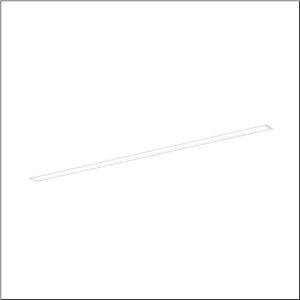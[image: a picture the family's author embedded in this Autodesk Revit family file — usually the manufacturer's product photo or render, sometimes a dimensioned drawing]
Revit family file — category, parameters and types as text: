
# Revit family: silica_21_51mx13tbt5w
name_source: partatom
category: Lighting Fixtures
units: mm (PartAtom-declared; Revit-internal decimal feet)

## family parameters
Cut with Voids When Loaded = No
Host = Face
Light Source = No
Part Type = Normal
Room Calculation Point = No
Round Connector Dimension = Use Diameter
Shared = No

## types (1)
- --- (1 x LED, 4030 lm, 40.5 W, 6500K)
    Apparent Load = 41 VA
    CIE Flux Codes = 78 96 99 100 100
    Color Rendering = 80
    Color Temperature = 6500K
    Default Elevation = 1800 mm
    Description = Silica 21, office luminaire, primary optical cover: prismatic diffuser, of PMMA, CAT 2 (L<= 3000cd/m²), light emission: direct distribution, primary light characteristic: symmetric, installation type: recessed, LED, rated luminous flux: 4.030lm, luminous efficacy: 95lm/W, light colour: 8tw, colour temperature: 2700..6500K, control gear: DALI DT8, with terminal, 3+2-pole, max. 2.5mm², mains connection: 220..240V, AC, 50/60Hz, rated input power: 42.6W, luminaire housing, of aluminium, traffic white (RAL 9016), length: 1.528mm, width: 79mm, height: 53mm, protection rating (complete): IP20, insulation class (complete): insulation class I (protective earthing), certification: CE, ENEC, VDE, permissible operating ambient temperature: 0..+35°C, standard: EN 50419, packaging unit: 1 piece
    Height = 0 mm  [stored 0 ft]
    Lamp = 1 x LED
    Lamp Light Flux = 4030 lm
    Lamp Power = 40.5 W
    Lamp count = 1
    Length = 1527 mm
    Luminous efficacy = 100 lm/W
    Manufacturer = Siteco
    ModVariant = No
    Model = 51MX13TBT5W
    Mounting Place = Ceiling
    Mounting Type = Recessed
    Number of Poles = 1
    OnlyDefault = Yes
    Power Factor = 1
    Product Name = Silica 21
    Product group = office luminaire | ceiling recessed
    ProductGroupID = 400
    Protection Class = Protection class I
    Protection Degree = IP 20
    RLX_Detail_Level = 1
    RLX_Emergency_Light_Flux = 0 lm
    RLX_Emergency_Type = 0
    RLX_Emergency_Type_DB = No
    RlxData = <blob elided: 10977 chars, md5=a58d0484>
    Socket = socket
    Standby Power = 0 W
    System Light Flux = 4030 lm
    System Power = 41 W
    Type Comments = individual setting
    Type Image = l_1251692.jpg
    URL = http://relux.com
    VarID = @adj_140899
    Voltage = 0 V
    Weight = 0.00 kg
    Width = 79 mm

note: [stored X ft] marks values corroborated as IEEE doubles in the binary element streams (Revit-internal decimal feet)

## geometry (parser evidence)
native form markers: Sweep x11
no freeform markers — native parametric forms only
